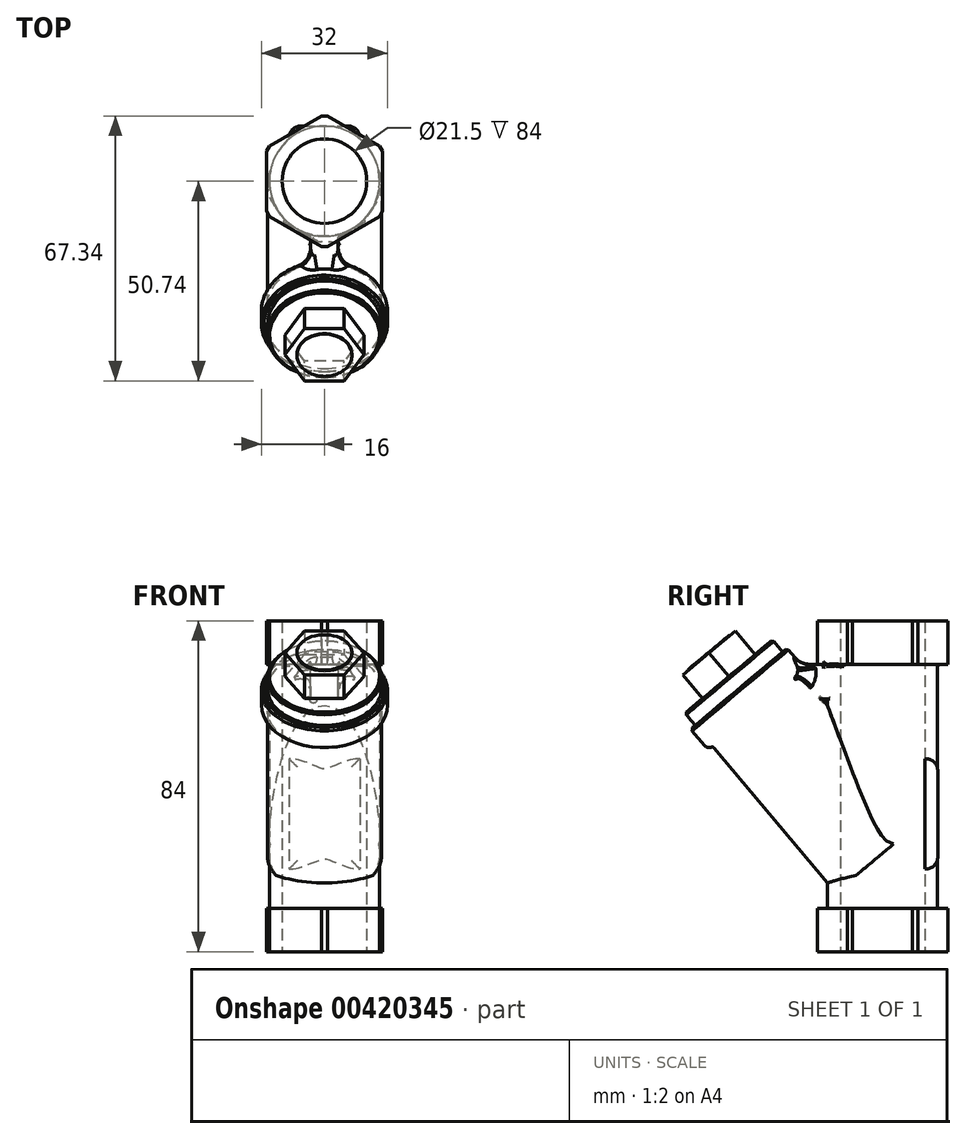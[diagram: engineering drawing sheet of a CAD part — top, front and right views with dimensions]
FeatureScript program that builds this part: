
annotation { "Feature Type Name" : "Feature", "Feature Type Description" : "" }
export const myFeature = defineFeature(function(context is Context, id is Id, definition is map)
    precondition{}
    {
        {
            var Q0;
            Q0=qCreatedBy(makeId("Top.planeOp"),FACE);
            var sketch = newSketch(context, id + "F0", { "sketchPlane" : qUnion([Q0])});
            skCircle(sketch, "E0", {"center": v(0, 0) * mm, "radius": 14 * mm});
            skSolve(sketch);
        }
        {
            var Q0;
            Q0 = qSketchRegion(id + "F0", true);
            extrude(context, id + "F1", {"entities" : qUnion([Q0]), "endBound" : BoundingType.SYMMETRIC, "depth" : 84 * mm});
        }
        {
            var Q0;
            Q0=qCreatedBy(makeId("Right.planeOp"),FACE);
            var sketch = newSketch(context, id + "F2", { "sketchPlane" : qUnion([Q0])});
            skLineSegment(sketch, "E1", {"start": v(-14, -42) * mm, "end": v(-14, 42) * mm, "construction": true});
            skLineSegment(sketch, "E2", {"start": v(14, 42) * mm, "end": v(14, -42) * mm, "construction": true});
            skLineSegment(sketch, "E3", {"start": v(-14, 42) * mm, "end": v(14, 42) * mm, "construction": true});
            skLineSegment(sketch, "E4", {"start": v(-14, -42) * mm, "end": v(14, -42) * mm, "construction": true});
            skLineSegment(sketch, "E5", {"start": v(-14, 0) * mm, "end": v(14, 0) * mm, "construction": true});
            skLineSegment(sketch, "E6", {"start": v(0, 42) * mm, "end": v(0, -42) * mm, "construction": true});
            skSolve(sketch);
        }
        {
            var Q0;
            Q0=makeQuery(id+"F1.opExtrude","CAP_FACE",FACE,{"disambiguationData":[OSD([sQuery(id+"F0.wireOp",EDGE,"E0")])],"isStart":true});
            var sketch = newSketch(context, id + "F3", { "sketchPlane" : qUnion([Q0])});
            skCircle(sketch, "E7.cCircle", {"center": v(0, 0) * mm, "radius": 17.03 * mm, "construction": true});
            skLineSegment(sketch, "E7.0", {"start": v(-14.75, 8.52) * mm, "end": v(0, 17.03) * mm});
            skLineSegment(sketch, "E7.1", {"start": v(0, 17.03) * mm, "end": v(14.75, 8.52) * mm});
            skLineSegment(sketch, "E7.2", {"start": v(14.75, 8.52) * mm, "end": v(14.75, -8.52) * mm});
            skLineSegment(sketch, "E7.3", {"start": v(14.75, -8.52) * mm, "end": v(0, -17.03) * mm});
            skLineSegment(sketch, "E7.4", {"start": v(0, -17.03) * mm, "end": v(-14.75, -8.52) * mm});
            skLineSegment(sketch, "E7.5", {"start": v(-14.75, -8.52) * mm, "end": v(-14.75, 8.52) * mm});
            skSolve(sketch);
        }
        {
            var Q0;
            Q0 = qSketchRegion(id + "F3", true);
            extrude(context, id + "F4", {"entities" : qUnion([Q0]), "operationType" : NewBodyOperationType.ADD, "oppositeDirection" : true, "depth" : 11 * mm});
        }
        {
            var Q0;
            Q0=makeQuery(id+"F1.opExtrude","SWEPT_BODY",BODY,{"disambiguationData":[OSD([sQuery(id+"F0.wireOp",EDGE,"E0")])]});
            var Q1;
            Q1=qCreatedBy(makeId("Top.planeOp"),FACE);
            mirror(context, id + "F5", {"operationType" : NewBodyOperationType.ADD, "entities" : qUnion([Q0]), "mirrorPlane" : qUnion([Q1])});
        }
        {
            var Q0;
            Q0=makeQuery(id+"F5.opPattern","COPY",EDGE,{"derivedFrom":makeQuery(id+"F4.opExtrude","SWEPT_EDGE",EDGE,{"disambiguationData":[OSD([sQuery(id+"F3.wireOp",EDGE,"E7.4"),sQuery(id+"F3.wireOp",EDGE,"E7.5")])]}),"instanceName":"1"});
            var Q1;
            Q1=makeQuery(id+"F5.opPattern","COPY",EDGE,{"derivedFrom":makeQuery(id+"F4.opExtrude","SWEPT_EDGE",EDGE,{"disambiguationData":[OSD([sQuery(id+"F3.wireOp",EDGE,"E7.3"),sQuery(id+"F3.wireOp",EDGE,"E7.4")])]}),"instanceName":"1"});
            var Q2;
            Q2=makeQuery(id+"F5.opPattern","COPY",EDGE,{"derivedFrom":makeQuery(id+"F4.opExtrude","SWEPT_EDGE",EDGE,{"disambiguationData":[OSD([sQuery(id+"F3.wireOp",EDGE,"E7.0"),sQuery(id+"F3.wireOp",EDGE,"E7.5")])]}),"instanceName":"1"});
            var Q3;
            Q3=makeQuery(id+"F4.opExtrude","SWEPT_EDGE",EDGE,{"disambiguationData":[OSD([sQuery(id+"F3.wireOp",EDGE,"E7.0"),sQuery(id+"F3.wireOp",EDGE,"E7.5")])]});
            var Q4;
            Q4=makeQuery(id+"F4.opExtrude","SWEPT_EDGE",EDGE,{"disambiguationData":[OSD([sQuery(id+"F3.wireOp",EDGE,"E7.4"),sQuery(id+"F3.wireOp",EDGE,"E7.5")])]});
            var Q5;
            Q5=makeQuery(id+"F4.opExtrude","SWEPT_EDGE",EDGE,{"disambiguationData":[OSD([sQuery(id+"F3.wireOp",EDGE,"E7.3"),sQuery(id+"F3.wireOp",EDGE,"E7.4")])]});
            var Q6;
            Q6=makeQuery(id+"F4.opExtrude","SWEPT_EDGE",EDGE,{"disambiguationData":[OSD([sQuery(id+"F3.wireOp",EDGE,"E7.0"),sQuery(id+"F3.wireOp",EDGE,"E7.1")])]});
            var Q7;
            Q7=makeQuery(id+"F5.opPattern","COPY",EDGE,{"derivedFrom":makeQuery(id+"F4.opExtrude","SWEPT_EDGE",EDGE,{"disambiguationData":[OSD([sQuery(id+"F3.wireOp",EDGE,"E7.0"),sQuery(id+"F3.wireOp",EDGE,"E7.1")])]}),"instanceName":"1"});
            var Q8;
            Q8=makeQuery(id+"F5.opPattern","COPY",EDGE,{"derivedFrom":makeQuery(id+"F4.opExtrude","SWEPT_EDGE",EDGE,{"disambiguationData":[OSD([sQuery(id+"F3.wireOp",EDGE,"E7.1"),sQuery(id+"F3.wireOp",EDGE,"E7.2")])]}),"instanceName":"1"});
            var Q9;
            Q9=makeQuery(id+"F4.opExtrude","SWEPT_EDGE",EDGE,{"disambiguationData":[OSD([sQuery(id+"F3.wireOp",EDGE,"E7.1"),sQuery(id+"F3.wireOp",EDGE,"E7.2")])]});
            var Q10;
            Q10=makeQuery(id+"F4.opExtrude","SWEPT_EDGE",EDGE,{"disambiguationData":[OSD([sQuery(id+"F3.wireOp",EDGE,"E7.2"),sQuery(id+"F3.wireOp",EDGE,"E7.3")])]});
            var Q11;
            Q11=makeQuery(id+"F5.opPattern","COPY",EDGE,{"derivedFrom":makeQuery(id+"F4.opExtrude","SWEPT_EDGE",EDGE,{"disambiguationData":[OSD([sQuery(id+"F3.wireOp",EDGE,"E7.2"),sQuery(id+"F3.wireOp",EDGE,"E7.3")])]}),"instanceName":"1"});
            chamfer(context, id + "F6", {"entities" : qUnion([Q0, Q1, Q2, Q3, Q4, Q5, Q6, Q7, Q8, Q9, Q10, Q11]), "width" : 1.5 * mm, "tangentPropagation" : true});
        }
        {
            var Q0;
            Q0=qCreatedBy(makeId("Front.planeOp"),FACE);
            cPlane(context, id + "F7", {"entities" : qUnion([Q0]), "cplaneType" : CPlaneType.OFFSET, "offset" : 14.03 * mm, "oppositeDirection" : true, "width" : 150 * mm, "height" : 150 * mm});
        }
        {
            var Q0;
            Q0=qCreatedBy(id+"F7.planeOp",FACE);
            var sketch = newSketch(context, id + "F8", { "sketchPlane" : qUnion([Q0])});
            skLineSegment(sketch, "E8.0", {"start": v(0, 31) * mm, "end": v(0, -31) * mm, "construction": true});
            skLineSegment(sketch, "E9.bottom", {"start": v(-9, 7) * mm, "end": v(9, 7) * mm});
            skLineSegment(sketch, "E9.top", {"start": v(-9, -21) * mm, "end": v(9, -21) * mm});
            skLineSegment(sketch, "E9.left", {"start": v(-9, 7) * mm, "end": v(-9, -21) * mm});
            skLineSegment(sketch, "E9.right", {"start": v(9, 7) * mm, "end": v(9, -21) * mm});
            skPoint(sketch, "E9.middle", {"position": v(0, -7) * mm});
            skLineSegment(sketch, "E10.0", {"start": v(-1.3, -42) * mm, "end": v(1.3, -42) * mm, "construction": true});
            skLineSegment(sketch, "E11.0", {"start": v(13.45, -31) * mm, "end": v(1.3, -31) * mm, "construction": true});
            skLineSegment(sketch, "E12.0", {"start": v(-1.3, -31) * mm, "end": v(-13.45, -31) * mm, "construction": true});
            skLineSegment(sketch, "E13.0", {"start": v(1.3, -31) * mm, "end": v(-1.3, -31) * mm, "construction": true});
            skLineSegment(sketch, "E14.0", {"start": v(-1.3, 31) * mm, "end": v(1.3, 31) * mm, "construction": true});
            skSolve(sketch);
        }
        {
            var Q0;
            Q0 = qSketchRegion(id + "F8", true);
            extrude(context, id + "F9", {"entities" : qUnion([Q0]), "operationType" : NewBodyOperationType.ADD, "depth" : 7.1 * mm});
        }
        {
            var Q0;
            Q0=qCreatedBy(makeId("Right.planeOp"),FACE);
            var sketch = newSketch(context, id + "F10", { "sketchPlane" : qUnion([Q0])});
            skLineSegment(sketch, "E15.0", {"start": v(0, 42) * mm, "end": v(0, -42) * mm, "construction": true});
            skLineSegment(sketch, "E16", {"start": v(14, -5.25) * mm, "end": v(-14, -28.75) * mm, "construction": true});
            skLineSegment(sketch, "E17.0", {"start": v(-14, -42) * mm, "end": v(-14, 42) * mm, "construction": true});
            skLineSegment(sketch, "E18.0", {"start": v(14, 42) * mm, "end": v(14, -42) * mm, "construction": true});
            skLineSegment(sketch, "E19", {"start": v(0, -42) * mm, "end": v(0, -17) * mm, "construction": true});
            skSolve(sketch);
        }
        {
            var Q0;
            Q0=sQuery(id+"F10.wireOp",EDGE,"E16");
            cPlane(context, id + "F11", {"entities" : qUnion([Q0]), "cplaneType" : CPlaneType.LINE_ANGLE, "offset" : 25 * mm, "angle" : 0 * degree, "width" : 150 * mm, "height" : 150 * mm});
        }
        {
            var Q0;
            Q0=qCreatedBy(id+"F11.planeOp",FACE);
            var sketch = newSketch(context, id + "F12", { "sketchPlane" : qUnion([Q0])});
            skCircle(sketch, "E20", {"center": v(0, 12) * mm, "radius": 14.5 * mm});
            skLineSegment(sketch, "E21.0", {"start": v(0, -27) * mm, "end": v(0, 27) * mm, "construction": true});
            skSolve(sketch);
        }
        {
            var Q0;
            Q0 = qSketchRegion(id + "F12", true);
            extrude(context, id + "F13", {"entities" : qUnion([Q0]), "operationType" : NewBodyOperationType.ADD, "oppositeDirection" : true, "depth" : 52 * mm});
        }
        {
            var Q0;
            Q0=qCreatedBy(makeId("Right.planeOp"),FACE);
            var sketch = newSketch(context, id + "F14", { "sketchPlane" : qUnion([Q0])});
            skLineSegment(sketch, "E22.0", {"start": v(-23.14, 31.47) * mm, "end": v(-45.35, 12.83) * mm, "construction": true});
            skLineSegment(sketch, "E23.0", {"start": v(14, -5.25) * mm, "end": v(-14, -28.75) * mm, "construction": true});
            skArc(sketch, "E24", {"start": v(-45.35, 12.83) * mm, "mid": v(-30.42, -8.76) * mm, "end": v(-10.38, -25.7) * mm});
            skLineSegment(sketch, "E25", {"start": v(-34.24, 22.15) * mm, "end": v(-0.82, -17.69) * mm, "construction": true});
            skLineSegment(sketch, "E26", {"start": v(-14, -24.54) * mm, "end": v(-46.64, 14.36) * mm});
            skSolve(sketch);
        }
        {
            var Q0;
            Q0 = qSketchRegion(id + "F14", true);
            var Q1;
            Q1=sQuery(id+"F14.wireOp",EDGE,"E24");
            var Q2;
            Q2=sQuery(id+"F14.wireOp",EDGE,"E25");
            revolve(context, id + "F15", {"bodyType" : ToolBodyType.SURFACE, "entities" : qUnion([Q0]), "surfaceEntities" : qUnion([Q1]), "axis" : qUnion([Q2]), "revolveType" : RevolveType.FULL});
        }
        {
            var Q0;
            Q0=makeQuery(id+"F13.opExtrude","CAP_FACE",FACE,{"disambiguationData":[OSD([sQuery(id+"F12.wireOp",EDGE,"E20")])],"isStart":false});
            var sketch = newSketch(context, id + "F16", { "sketchPlane" : qUnion([Q0])});
            skCircle(sketch, "E27", {"center": v(0, -12) * mm, "radius": 16 * mm});
            skSolve(sketch);
        }
        {
            var Q0;
            Q0 = qSketchRegion(id + "F16", true);
            extrude(context, id + "F17", {"entities" : qUnion([Q0]), "operationType" : NewBodyOperationType.ADD, "endBound" : BoundingType.SYMMETRIC, "depth" : 7 * mm});
        }
        {
            var Q0;
            Q0=makeQuery(id+"F17.opExtrude","CAP_EDGE",EDGE,{"disambiguationData":[OSD([sQuery(id+"F16.wireOp",EDGE,"E27")])],"isStart":true});
            var Q1;
            Q1=makeQuery(id+"F15.opRevolve","SWEPT_FACE",FACE,{"disambiguationData":[OSD([sQuery(id+"F14.wireOp",EDGE,"E24")])]});
            fillet(context, id + "F18", {"entities" : qUnion([Q0, Q1]), "radius" : 1.6 * mm, "tangentPropagation" : true, "allowEdgeOverflow" : false});
        }
        {
            var Q0;
            Q0=makeQuery(id+"F17.opExtrude","CAP_EDGE",EDGE,{"disambiguationData":[OSD([sQuery(id+"F16.wireOp",EDGE,"E27")])],"isStart":false});
            chamfer(context, id + "F19", {"entities" : qUnion([Q0]), "width" : 0.6 * mm, "tangentPropagation" : true});
        }
        {
            var Q0;
            Q0=makeQuery(id+"F17.opExtrude","CAP_FACE",FACE,{"disambiguationData":[OSD([sQuery(id+"F16.wireOp",EDGE,"E27")])],"isStart":false});
            var sketch = newSketch(context, id + "F20", { "sketchPlane" : qUnion([Q0])});
            skCircle(sketch, "E28", {"center": v(0, -12) * mm, "radius": 14.5 * mm});
            skSolve(sketch);
        }
        {
            var Q0;
            Q0 = qSketchRegion(id + "F20", true);
            extrude(context, id + "F21", {"entities" : qUnion([Q0]), "depth" : 4 * mm});
        }
        {
            var Q0;
            Q0=makeQuery(id+"F21.opExtrude","CAP_FACE",FACE,{"disambiguationData":[OSD([sQuery(id+"F20.wireOp",EDGE,"E28")])],"isStart":false});
            chamfer(context, id + "F22", {"entities" : qUnion([Q0]), "width" : .5 * mm, "tangentPropagation" : true});
        }
        {
            var Q0;
            Q0=makeQuery(id+"F21.opExtrude","CAP_FACE",FACE,{"disambiguationData":[OSD([sQuery(id+"F20.wireOp",EDGE,"E28")])],"isStart":false});
            var sketch = newSketch(context, id + "F23", { "sketchPlane" : qUnion([Q0])});
            skCircle(sketch, "E29.cCircle", {"center": v(0, -12) * mm, "radius": 8.7 * mm, "construction": true});
            skLineSegment(sketch, "E29.0", {"start": v(5.02, -20.7) * mm, "end": v(-5.02, -20.7) * mm});
            skLineSegment(sketch, "E29.1", {"start": v(-5.02, -20.7) * mm, "end": v(-10.05, -12) * mm});
            skLineSegment(sketch, "E29.2", {"start": v(-10.05, -12) * mm, "end": v(-5.02, -3.3) * mm});
            skLineSegment(sketch, "E29.3", {"start": v(-5.02, -3.3) * mm, "end": v(5.02, -3.3) * mm});
            skLineSegment(sketch, "E29.4", {"start": v(5.02, -3.3) * mm, "end": v(10.05, -12) * mm});
            skLineSegment(sketch, "E29.5", {"start": v(10.05, -12) * mm, "end": v(5.02, -20.7) * mm});
            skPoint(sketch, "E29.0.midPoint", {"position": v(0, -20.7) * mm});
            skSolve(sketch);
        }
        {
            var Q0;
            Q0 = qSketchRegion(id + "F23", true);
            extrude(context, id + "F24", {"entities" : qUnion([Q0]), "operationType" : NewBodyOperationType.ADD, "depth" : 7.8 * mm});
        }
        {
            var Q0;
            Q0=makeQuery(id+"F24.opExtrude","CAP_FACE",FACE,{"disambiguationData":[OSD([sQuery(id+"F23.wireOp",EDGE,"E29.0"),sQuery(id+"F23.wireOp",EDGE,"E29.1"),sQuery(id+"F23.wireOp",EDGE,"E29.2"),sQuery(id+"F23.wireOp",EDGE,"E29.3"),sQuery(id+"F23.wireOp",EDGE,"E29.4"),sQuery(id+"F23.wireOp",EDGE,"E29.5")])],"isStart":false});
            var sketch = newSketch(context, id + "F25", { "sketchPlane" : qUnion([Q0])});
            skCircle(sketch, "E30.0", {"center": v(0, -12) * mm, "radius": 14 * mm, "construction": true});
            skCircle(sketch, "E31", {"center": v(0, -12) * mm, "radius": 7 * mm});
            skSolve(sketch);
        }
        {
            var Q0;
            Q0 = qSketchRegion(id + "F25", true);
            extrude(context, id + "F26", {"entities" : qUnion([Q0]), "operationType" : NewBodyOperationType.ADD, "depth" : .2 * mm});
        }
        {
            var Q0;
            Q0=qCreatedBy(makeId("Right.planeOp"),FACE);
            var sketch = newSketch(context, id + "F27", { "sketchPlane" : qUnion([Q0])});
            skLineSegment(sketch, "E32", {"start": v(-13.35, 31) * mm, "end": v(-21.3, 31) * mm});
            skLineSegment(sketch, "E33", {"start": v(-21.3, 31) * mm, "end": v(-21.3, 22.21) * mm});
            skLineSegment(sketch, "E34", {"start": v(-21.3, 22.21) * mm, "end": v(-13.35, 22.21) * mm});
            skLineSegment(sketch, "E35", {"start": v(-13.35, 22.21) * mm, "end": v(-13.35, 31) * mm});
            skLineSegment(sketch, "E36", {"start": v(-14, -31) * mm, "end": v(-14, 30.5) * mm, "construction": true});
            skLineSegment(sketch, "E37.0.0", {"start": v(-9.27, 31) * mm, "end": v(-16.28, 31) * mm, "construction": true});
            skLineSegment(sketch, "E37.0.1", {"start": v(-16.28, 31) * mm, "end": v(-16.28, 42) * mm, "construction": true});
            skLineSegment(sketch, "E37.0.2", {"start": v(-16.28, 42) * mm, "end": v(-9.27, 42) * mm, "construction": true});
            skLineSegment(sketch, "E37.0.3", {"start": v(-9.27, 42) * mm, "end": v(-9.27, 31) * mm, "construction": true});
            skSolve(sketch);
        }
        {
            var Q0;
            Q0 = qSketchRegion(id + "F27", true);
            extrude(context, id + "F28", {"entities" : qUnion([Q0]), "operationType" : NewBodyOperationType.ADD, "endBound" : BoundingType.SYMMETRIC, "depth" : 7 * mm});
        }
        {
            var Q0;
            {var subQ0=sQuery(id+"F27.wireOp",EDGE,"E32");Q0=makeQuery(id+"F28.boolean.opBoolean","SPLIT",EDGE,{"disambiguationData":[topologyDisambiguationEdgeConnected([makeQuery(id+"F28.opExtrude","SWEPT_FACE",FACE,{"disambiguationData":[OSD([subQ0])]})])],"derivedFrom":makeQuery(id+"F28.opExtrude","CAP_EDGE",EDGE,{"disambiguationData":[OSD([subQ0])],"isStart":false})});}
            var Q1;
            Q1=makeQuery(id+"F28.boolean.opBoolean","INTERSECT",EDGE,{"derivedFrom":[makeQuery(id+"F1.opExtrude","SWEPT_FACE",FACE,{"disambiguationData":[OSD([sQuery(id+"F0.wireOp",EDGE,"E0")])]}),makeQuery(id+"F28.opExtrude","CAP_FACE",FACE,{"disambiguationData":[OSD([sQuery(id+"F27.wireOp",EDGE,"E32"),sQuery(id+"F27.wireOp",EDGE,"E33"),sQuery(id+"F27.wireOp",EDGE,"E34"),sQuery(id+"F27.wireOp",EDGE,"E35")])],"isStart":false})]});
            var Q2;
            Q2=makeQuery(id+"F28.boolean.opBoolean","INTERSECT",EDGE,{"derivedFrom":[makeQuery(id+"F1.opExtrude","SWEPT_FACE",FACE,{"disambiguationData":[OSD([sQuery(id+"F0.wireOp",EDGE,"E0")])]}),makeQuery(id+"F28.opExtrude","CAP_FACE",FACE,{"disambiguationData":[OSD([sQuery(id+"F27.wireOp",EDGE,"E32"),sQuery(id+"F27.wireOp",EDGE,"E33"),sQuery(id+"F27.wireOp",EDGE,"E34"),sQuery(id+"F27.wireOp",EDGE,"E35")])],"isStart":true})]});
            var Q3;
            {var subQ0=sQuery(id+"F27.wireOp",EDGE,"E32");Q3=makeQuery(id+"F28.boolean.opBoolean","SPLIT",EDGE,{"disambiguationData":[topologyDisambiguationEdgeConnected([makeQuery(id+"F28.opExtrude","SWEPT_FACE",FACE,{"disambiguationData":[OSD([subQ0])]})])],"derivedFrom":makeQuery(id+"F28.opExtrude","CAP_EDGE",EDGE,{"disambiguationData":[OSD([subQ0])],"isStart":true})});}
            fillet(context, id + "F29", {"entities" : qUnion([Q0, Q1, Q2, Q3]), "radius" : 1 * mm, "tangentPropagation" : true, "allowEdgeOverflow" : false});
        }
        {
            var Q0;
            Q0=makeQuery(id+"F28.boolean.opBoolean","INTERSECT",EDGE,{"derivedFrom":[makeQuery(id+"F17.opExtrude","SWEPT_FACE",FACE,{"disambiguationData":[OSD([sQuery(id+"F16.wireOp",EDGE,"E27")])]}),makeQuery(id+"F28.opExtrude","SWEPT_FACE",FACE,{"disambiguationData":[OSD([sQuery(id+"F27.wireOp",EDGE,"E32")])]})]});
            fillet(context, id + "F30", {"entities" : qUnion([Q0]), "radius" : 5 * mm, "tangentPropagation" : true, "allowEdgeOverflow" : false});
        }
        {
            var Q0;
            {var subQ0=sQuery(id+"F3.wireOp",EDGE,"E7.1");var subQ1=sQuery(id+"F3.wireOp",EDGE,"E7.0");Q0=makeQuery(id+"F6.opChamfer","BLEND_EDGE",EDGE,{"blendedFrom":[makeQuery(id+"F5.opPattern","COPY",EDGE,{"derivedFrom":makeQuery(id+"F4.opExtrude","SWEPT_EDGE",EDGE,{"disambiguationData":[OSD([subQ1,subQ0])]}),"instanceName":"1"}),makeQuery(id+"F5.opPattern","COPY",FACE,{"derivedFrom":makeQuery(id+"F4.opExtrude","CAP_FACE",FACE,{"disambiguationData":[OSD([subQ1,subQ0,sQuery(id+"F3.wireOp",EDGE,"E7.2"),sQuery(id+"F3.wireOp",EDGE,"E7.3"),sQuery(id+"F3.wireOp",EDGE,"E7.4"),sQuery(id+"F3.wireOp",EDGE,"E7.5")])],"isStart":false}),"instanceName":"1"})],"blendedInto":[makeQuery(id+"F5.opPattern","COPY",FACE,{"derivedFrom":makeQuery(id+"F4.opExtrude","CAP_FACE",FACE,{"disambiguationData":[OSD([subQ1,subQ0,sQuery(id+"F3.wireOp",EDGE,"E7.2"),sQuery(id+"F3.wireOp",EDGE,"E7.3"),sQuery(id+"F3.wireOp",EDGE,"E7.4"),sQuery(id+"F3.wireOp",EDGE,"E7.5")])],"isStart":false}),"instanceName":"1"})]});}
            var Q1;
            {var subQ0=sQuery(id+"F3.wireOp",EDGE,"E7.1");Q1=makeQuery(id+"F28.boolean.opBoolean","SPLIT",EDGE,{"disambiguationData":[topologyDisambiguationEdgeConnected([makeQuery(id+"F28.opExtrude","SWEPT_FACE",FACE,{"disambiguationData":[OSD([sQuery(id+"F27.wireOp",EDGE,"E32")])]})])],"derivedFrom":makeQuery(id+"F5.opPattern","COPY",EDGE,{"derivedFrom":makeQuery(id+"F4.opExtrude","CAP_EDGE",EDGE,{"disambiguationData":[OSD([subQ0])],"isStart":false}),"instanceName":"1"})});}
            var Q2;
            {var subQ0=sQuery(id+"F3.wireOp",EDGE,"E7.0");Q2=makeQuery(id+"F28.boolean.opBoolean","SPLIT",EDGE,{"disambiguationData":[topologyDisambiguationEdgeConnected([makeQuery(id+"F28.opExtrude","SWEPT_FACE",FACE,{"disambiguationData":[OSD([sQuery(id+"F27.wireOp",EDGE,"E32")])]})])],"derivedFrom":makeQuery(id+"F5.opPattern","COPY",EDGE,{"derivedFrom":makeQuery(id+"F4.opExtrude","CAP_EDGE",EDGE,{"disambiguationData":[OSD([subQ0])],"isStart":false}),"instanceName":"1"})});}
            fillet(context, id + "F31", {"entities" : qUnion([Q0, Q1, Q2]), "radius" : 0.7 * mm, "tangentPropagation" : true, "allowEdgeOverflow" : false});
        }
        {
            var Q0;
            Q0=makeQuery(id+"F28.opExtrude","CAP_FACE",FACE,{"disambiguationData":[OSD([sQuery(id+"F27.wireOp",EDGE,"E32"),sQuery(id+"F27.wireOp",EDGE,"E33"),sQuery(id+"F27.wireOp",EDGE,"E34"),sQuery(id+"F27.wireOp",EDGE,"E35")])],"isStart":true});
            var Q1;
            {var subQ0=sQuery(id+"F27.wireOp",EDGE,"E35");var subQ1=sQuery(id+"F27.wireOp",EDGE,"E34");var subQ2=sQuery(id+"F27.wireOp",EDGE,"E33");var subQ3=sQuery(id+"F27.wireOp",EDGE,"E32");var subQ4=sQuery(id+"F16.wireOp",EDGE,"E27");Q1=makeQuery(id+"F30.opFillet","BLEND_FACE",FACE,{"disambiguationData":[OSD([subQ4,subQ3,subQ2,subQ1,subQ0]),TDD([makeQuery(id+"F28.boolean.opBoolean","INTERSECT",EDGE,{"derivedFrom":[makeQuery(id+"F18.opFillet","BLEND_FACE",FACE,{"disambiguationData":[OSD([subQ4])]}),makeQuery(id+"F28.opExtrude","CAP_FACE",FACE,{"disambiguationData":[OSD([subQ3,subQ2,subQ1,subQ0])],"isStart":true})]})])]});}
            fillet(context, id + "F32", {"entities" : qUnion([Q0, Q1]), "radius" : 0.6 * mm, "tangentPropagation" : true, "allowEdgeOverflow" : false});
        }
        {
            var Q0;
            Q0=makeQuery(id+"F9.opExtrude","CAP_FACE",FACE,{"disambiguationData":[OSD([sQuery(id+"F8.wireOp",EDGE,"E9.bottom"),sQuery(id+"F8.wireOp",EDGE,"E9.top"),sQuery(id+"F8.wireOp",EDGE,"E9.left"),sQuery(id+"F8.wireOp",EDGE,"E9.right")])],"isStart":true});
            fillet(context, id + "F33", {"entities" : qUnion([Q0]), "radius" : 3 * mm, "tangentPropagation" : true, "allowEdgeOverflow" : false});
        }
        {
            var Q0;
            Q0=makeQuery(id+"F4.boolean.opBoolean","MERGE",FACE,{"derivedFrom":[makeQuery(id+"F1.opExtrude","CAP_FACE",FACE,{"disambiguationData":[OSD([sQuery(id+"F0.wireOp",EDGE,"E0")])],"isStart":true}),makeQuery(id+"F4.opExtrude","CAP_FACE",FACE,{"disambiguationData":[OSD([sQuery(id+"F3.wireOp",EDGE,"E7.0"),sQuery(id+"F3.wireOp",EDGE,"E7.1"),sQuery(id+"F3.wireOp",EDGE,"E7.2"),sQuery(id+"F3.wireOp",EDGE,"E7.3"),sQuery(id+"F3.wireOp",EDGE,"E7.4"),sQuery(id+"F3.wireOp",EDGE,"E7.5")])],"isStart":true})]});
            var sketch = newSketch(context, id + "F34", { "sketchPlane" : qUnion([Q0])});
            skLineSegment(sketch, "E38.0.0", {"start": v(14.75, 7.02) * mm, "end": v(14.75, -7.02) * mm});
            skLineSegment(sketch, "E38.0.1", {"start": v(14.75, -7.02) * mm, "end": v(13.45, -9.27) * mm});
            skLineSegment(sketch, "E38.0.2", {"start": v(13.45, -9.27) * mm, "end": v(1.3, -16.28) * mm});
            skLineSegment(sketch, "E38.0.3", {"start": v(1.3, -16.28) * mm, "end": v(-1.3, -16.28) * mm});
            skLineSegment(sketch, "E38.0.4", {"start": v(-1.3, -16.28) * mm, "end": v(-13.45, -9.27) * mm});
            skLineSegment(sketch, "E38.0.5", {"start": v(-13.45, -9.27) * mm, "end": v(-14.75, -7.02) * mm});
            skLineSegment(sketch, "E38.0.6", {"start": v(-14.75, -7.02) * mm, "end": v(-14.75, 7.02) * mm});
            skLineSegment(sketch, "E38.0.7", {"start": v(-14.75, 7.02) * mm, "end": v(-13.45, 9.27) * mm});
            skLineSegment(sketch, "E38.0.8", {"start": v(-13.45, 9.27) * mm, "end": v(-1.3, 16.28) * mm});
            skLineSegment(sketch, "E38.0.9", {"start": v(-1.3, 16.28) * mm, "end": v(1.3, 16.28) * mm});
            skLineSegment(sketch, "E38.0.10", {"start": v(1.3, 16.28) * mm, "end": v(13.45, 9.27) * mm});
            skLineSegment(sketch, "E38.0.11", {"start": v(13.45, 9.27) * mm, "end": v(14.75, 7.02) * mm});
            skCircle(sketch, "E39", {"center": v(0, 0) * mm, "radius": 10.75 * mm});
            skPoint(sketch, "E39.centerSnap0", {"position": v(0, -16.28) * mm});
            skPoint(sketch, "E39.centerSnap1", {"position": v(-14.75, 0) * mm});
            skSolve(sketch);
        }
        {
            var Q0;
            Q0=makeQuery(id+"F34.imprint","IMPRINT",FACE,{"disambiguationData":[TD([[makeQuery(id+"F34.imprint","IMPRINT",EDGE,{"derivedFrom":sQuery(id+"F34.wireOp",EDGE,"E39")}),1.0]])]});
            extrude(context, id + "F35", {"entities" : qUnion([Q0]), "operationType" : NewBodyOperationType.REMOVE, "oppositeDirection" : true, "depth" : 100.8 * mm});
        }
    });
